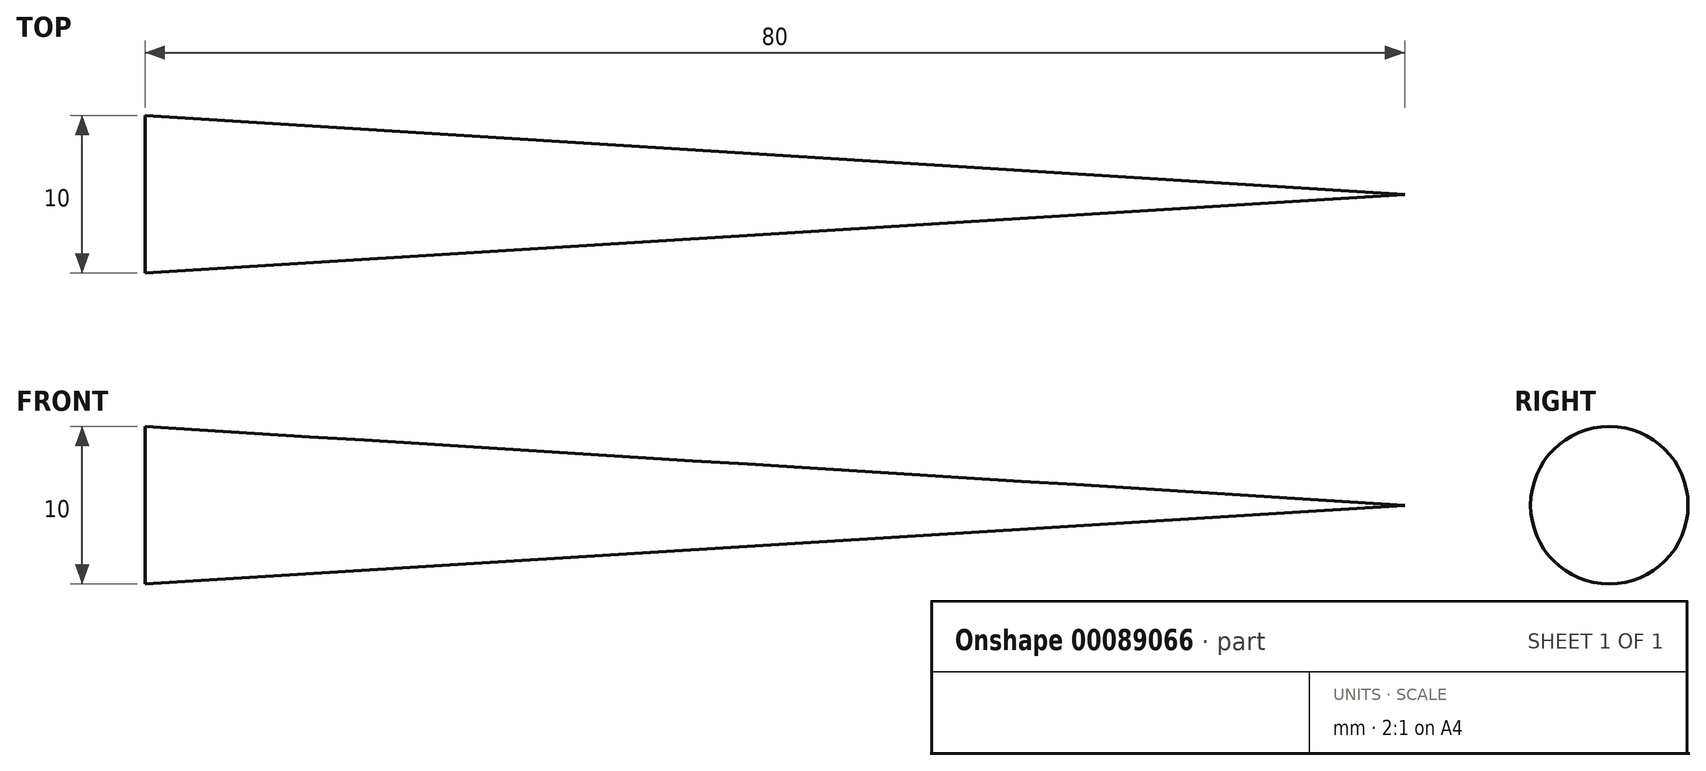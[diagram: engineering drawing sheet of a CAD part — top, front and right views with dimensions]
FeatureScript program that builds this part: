
annotation { "Feature Type Name" : "Feature", "Feature Type Description" : "" }
export const myFeature = defineFeature(function(context is Context, id is Id, definition is map)
    precondition{}
    {
        {
            var Q0;
            Q0=qCreatedBy(makeId("Top.planeOp"),FACE);
            var sketch = newSketch(context, id + "F0", { "sketchPlane" : qUnion([Q0])});
            skLineSegment(sketch, "E0", {"start": v(0, 0) * mm, "end": v(80, 0) * mm});
            skLineSegment(sketch, "E1", {"start": v(80, 0) * mm, "end": v(0, 5) * mm});
            skLineSegment(sketch, "E2", {"start": v(0, 5) * mm, "end": v(0, 0) * mm});
            skSolve(sketch);
        }
        {
            var Q0;
            Q0=makeQuery(id+"F0.imprint","IMPRINT",FACE,{"disambiguationData":[TD([[makeQuery(id+"F0.imprint","IMPRINT",EDGE,{"derivedFrom":sQuery(id+"F0.wireOp",EDGE,"E0")}),1.0]])]});
            var Q1;
            Q1=sQuery(id+"F0.wireOp",EDGE,"E0");
            revolve(context, id + "F1", {"entities" : qUnion([Q0]), "axis" : qUnion([Q1]), "revolveType" : RevolveType.FULL});
        }
    });
